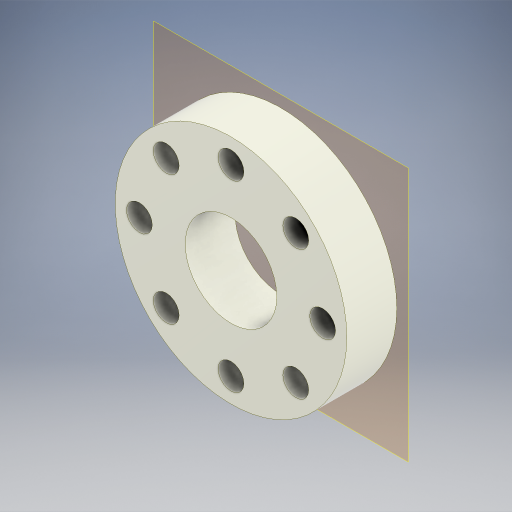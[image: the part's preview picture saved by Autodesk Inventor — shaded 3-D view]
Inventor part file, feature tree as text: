
AUTODESK INVENTOR PART (.ipt)
format: ipt  version: 2024 (Build 280153000, 153)  size: 294,912 bytes
history: native  units: in
note: dims shown in document units (in); Inventor stores cm internally (conversion verified against a paired STEP export)
features: other x4, extrude x1, sketch x1, reference x1
ambient origin geometry x8: Origin, YZ Plane, XZ Plane, XY Plane, X Axis, Y Axis, Z Axis, Center Point
bodies: Body1 (feature_tree)
feature tree (7):
  other  "솔리드1"
  other  "작업 평면1"
  extrude  "돌출1"  Depth=0.0197in
  sketch  "스케치1"
  reference  "참조1"
  other  "조립품17"
  other  "64-106Horn:1"
